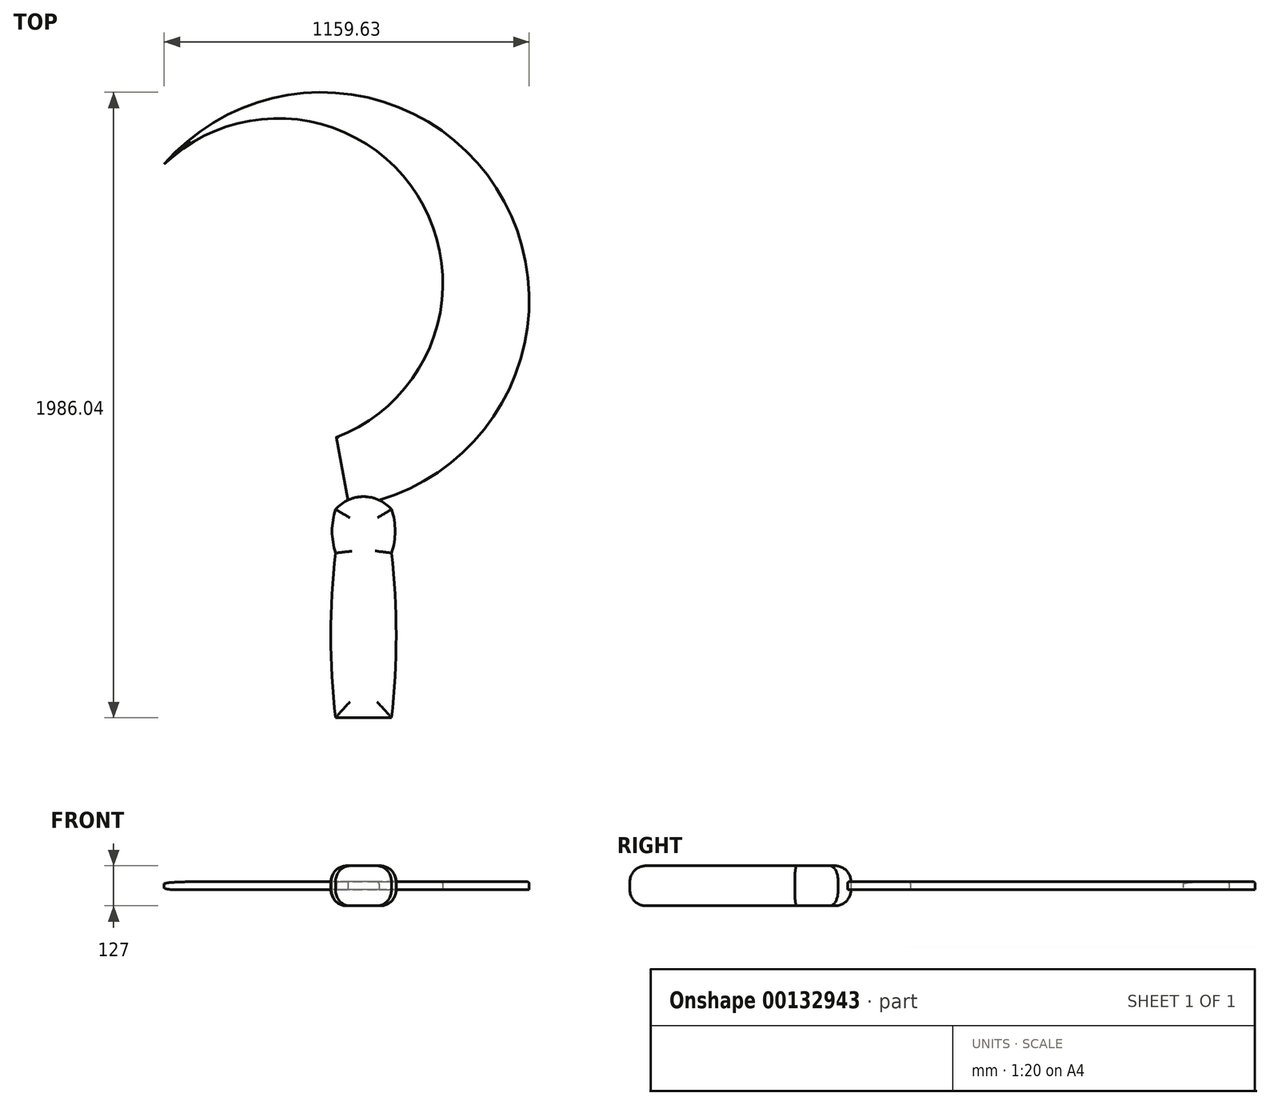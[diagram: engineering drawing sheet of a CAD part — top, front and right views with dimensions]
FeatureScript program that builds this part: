
annotation { "Feature Type Name" : "Feature", "Feature Type Description" : "" }
export const myFeature = defineFeature(function(context is Context, id is Id, definition is map)
    precondition{}
    {
        {
            var Q0;
            Q0=qCreatedBy(makeId("Top.planeOp"),FACE);
            var sketch = newSketch(context, id + "F0", { "sketchPlane" : qUnion([Q0])});
            skLineSegment(sketch, "E0", {"start": v(102.64, -741) * mm, "end": v(-75.16, -741) * mm});
            skPoint(sketch, "E1", {"position": v(-75.16, -217.55) * mm});
            skPoint(sketch, "E2", {"position": v(102.64, -217.55) * mm});
            skPoint(sketch, "E3", {"position": v(-75.16, -79.41) * mm});
            skPoint(sketch, "E4", {"position": v(102.64, -79.41) * mm});
            skArc(sketch, "E5", {"start": v(-75.16, -217.55) * mm, "mid": v(-90.02, -479.27) * mm, "end": v(-75.16, -741) * mm});
            skArc(sketch, "E6", {"start": v(102.64, -741) * mm, "mid": v(117.5, -479.27) * mm, "end": v(102.64, -217.55) * mm});
            skArc(sketch, "E7", {"start": v(-75.16, -79.41) * mm, "mid": v(-86.01, -148.48) * mm, "end": v(-75.16, -217.55) * mm});
            skArc(sketch, "E8", {"start": v(102.64, -217.55) * mm, "mid": v(114.28, -148.48) * mm, "end": v(102.64, -79.41) * mm});
            skArc(sketch, "E9", {"start": v(102.64, -79.41) * mm, "mid": v(13.74, -38.74) * mm, "end": v(-75.16, -79.41) * mm});
            skSolve(sketch);
        }
        {
            var Q0;
            Q0=makeQuery(id+"F0.imprint","IMPRINT",FACE,{"disambiguationData":[TD([[makeQuery(id+"F0.imprint","IMPRINT",EDGE,{"derivedFrom":sQuery(id+"F0.wireOp",EDGE,"E0")}),-1.0]])]});
            extrude(context, id + "F1", {"entities" : qUnion([Q0]), "endBound" : BoundingType.SYMMETRIC, "depth" : 127 * mm});
        }
        {
            var Q0;
            Q0=makeQuery(id+"F1.opExtrude","CAP_FACE",FACE,{"disambiguationData":[OSD([sQuery(id+"F0.wireOp",EDGE,"E0"),sQuery(id+"F0.wireOp",EDGE,"E5"),sQuery(id+"F0.wireOp",EDGE,"E6"),sQuery(id+"F0.wireOp",EDGE,"E7"),sQuery(id+"F0.wireOp",EDGE,"E8"),sQuery(id+"F0.wireOp",EDGE,"E9")])],"isStart":false});
            var Q1;
            Q1=makeQuery(id+"F1.opExtrude","CAP_FACE",FACE,{"disambiguationData":[OSD([sQuery(id+"F0.wireOp",EDGE,"E0"),sQuery(id+"F0.wireOp",EDGE,"E5"),sQuery(id+"F0.wireOp",EDGE,"E6"),sQuery(id+"F0.wireOp",EDGE,"E7"),sQuery(id+"F0.wireOp",EDGE,"E8"),sQuery(id+"F0.wireOp",EDGE,"E9")])],"isStart":true});
            fillet(context, id + "F2", {"entities" : qUnion([Q0, Q1]), "radius" : 50.8 * mm, "tangentPropagation" : true, "allowEdgeOverflow" : false});
        }
        {
            var Q0;
            Q0=qCreatedBy(makeId("Top.planeOp"),FACE);
            var sketch = newSketch(context, id + "F3", { "sketchPlane" : qUnion([Q0])});
            skArc(sketch, "E10.0", {"start": v(-75.16, -79.41) * mm, "mid": v(13.74, -38.74) * mm, "end": v(102.64, -79.41) * mm});
            skLineSegment(sketch, "E11", {"start": v(-36.22, -49.9) * mm, "end": v(-73.03, 149.94) * mm});
            skPoint(sketch, "E12", {"position": v(-619.57, 1016.68) * mm});
            skArc(sketch, "E13", {"start": v(62.93, -49.53) * mm, "mid": v(435.9, 940.75) * mm, "end": v(-619.57, 1016.68) * mm});
            skArc(sketch, "E14", {"start": v(-73.03, 149.94) * mm, "mid": v(185.03, 918.35) * mm, "end": v(-619.57, 1016.68) * mm});
            skSolve(sketch);
        }
        {
            var Q0;
            {var subQ0=sQuery(id+"F3.wireOp",EDGE,"E11");Q0=makeQuery(id+"F3.imprint","IMPRINT",FACE,{"disambiguationData":[TD([[makeQuery(id+"F3.imprint","IMPRINT",EDGE,{"derivedFrom":subQ0}),-1.0]])]});}
            extrude(context, id + "F4", {"entities" : qUnion([Q0]), "endBound" : BoundingType.SYMMETRIC, "depth" : 25.4 * mm});
        }
        {
            var Q0;
            Q0=makeQuery(id+"F4.opExtrude","CAP_EDGE",EDGE,{"disambiguationData":[OSD([sQuery(id+"F3.wireOp",EDGE,"E14")])],"isStart":false});
            var Q1;
            Q1=makeQuery(id+"F4.opExtrude","CAP_EDGE",EDGE,{"disambiguationData":[OSD([sQuery(id+"F3.wireOp",EDGE,"E13")])],"isStart":false});
            var Q2;
            Q2=makeQuery(id+"F4.opExtrude","CAP_EDGE",EDGE,{"disambiguationData":[OSD([sQuery(id+"F3.wireOp",EDGE,"E14")])],"isStart":true});
            var Q3;
            Q3=makeQuery(id+"F4.opExtrude","CAP_EDGE",EDGE,{"disambiguationData":[OSD([sQuery(id+"F3.wireOp",EDGE,"E11")])],"isStart":false});
            var Q4;
            Q4=makeQuery(id+"F4.opExtrude","CAP_EDGE",EDGE,{"disambiguationData":[OSD([sQuery(id+"F3.wireOp",EDGE,"E11")])],"isStart":true});
            fillet(context, id + "F5", {"entities" : qUnion([Q0, Q1, Q2, Q3, Q4]), "radius" : 6.35 * mm, "tangentPropagation" : true, "allowEdgeOverflow" : false});
        }
    });
